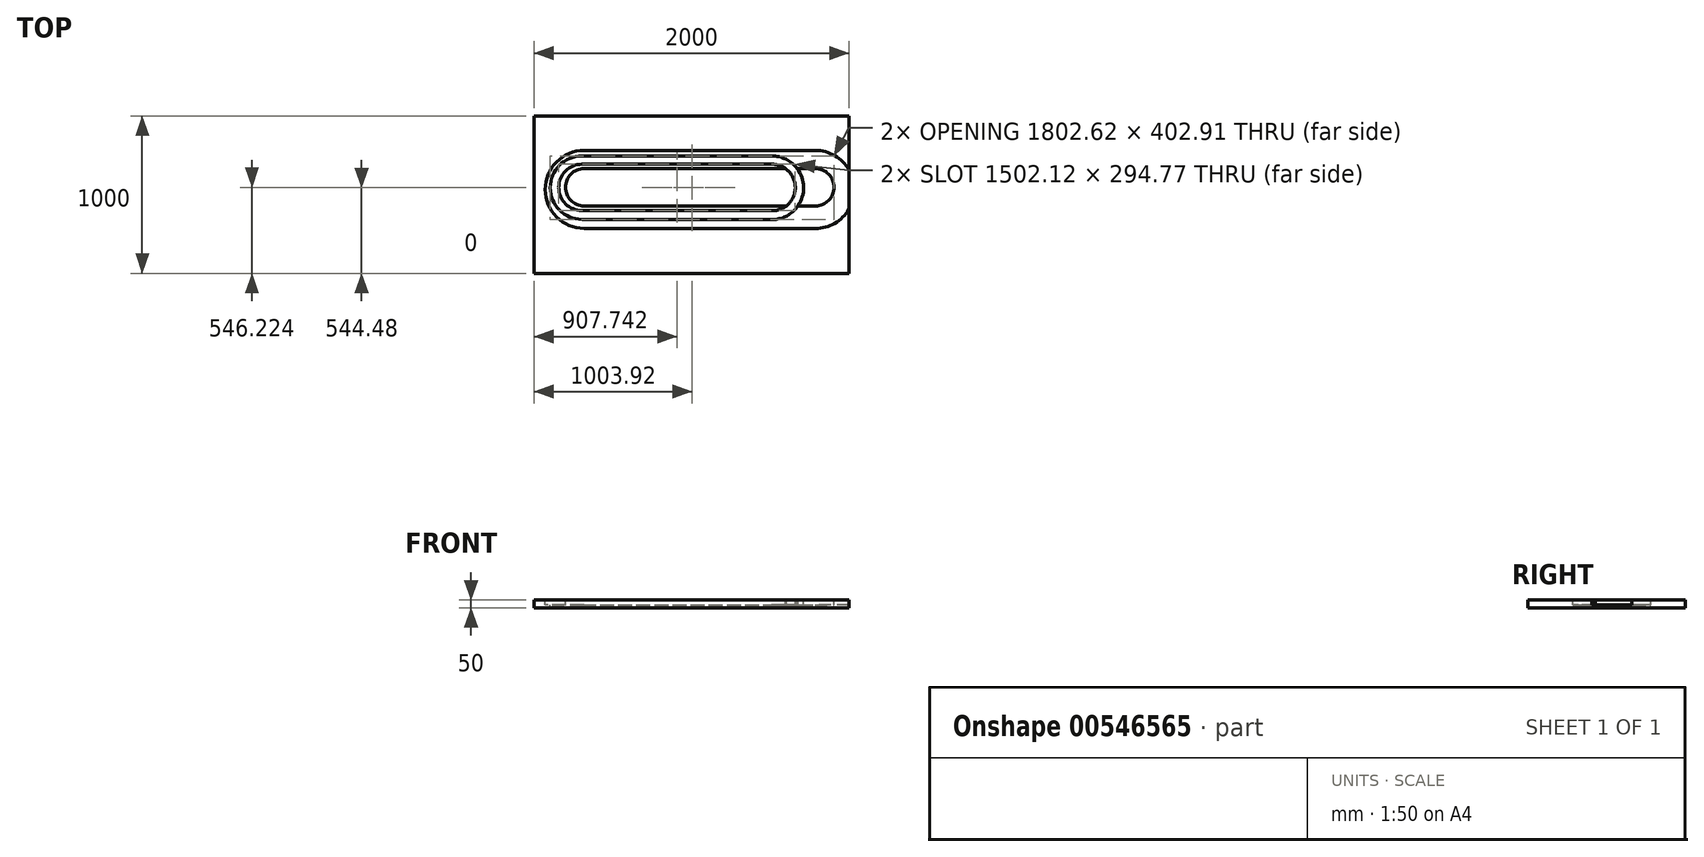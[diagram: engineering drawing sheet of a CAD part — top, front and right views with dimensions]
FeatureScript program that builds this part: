
annotation { "Feature Type Name" : "Feature", "Feature Type Description" : "" }
export const myFeature = defineFeature(function(context is Context, id is Id, definition is map)
    precondition{}
    {
        {
            var Q0;
            Q0=qCreatedBy(makeId("Top.planeOp"),FACE);
            var sketch = newSketch(context, id + "F0", { "sketchPlane" : qUnion([Q0])});
            skLineSegment(sketch, "E0.bottom", {"start": v(-970.21, 444.4) * mm, "end": v(1029.79, 444.4) * mm});
            skLineSegment(sketch, "E0.top", {"start": v(-970.21, -555.6) * mm, "end": v(1029.79, -555.6) * mm});
            skLineSegment(sketch, "E0.left", {"start": v(-970.21, 444.4) * mm, "end": v(-970.21, -555.6) * mm});
            skLineSegment(sketch, "E0.right", {"start": v(1029.79, 444.4) * mm, "end": v(1029.79, -555.6) * mm});
            skSolve(sketch);
        }
        {
            var Q0;
            Q0=makeQuery(id+"F0.imprint","IMPRINT",FACE,{"disambiguationData":[TD([[makeQuery(id+"F0.imprint","IMPRINT",EDGE,{"derivedFrom":sQuery(id+"F0.wireOp",EDGE,"E0.bottom")}),-1.0]])]});
            extrude(context, id + "F1", {"entities" : qUnion([Q0]), "depth" : 50 * mm, "offsetDistance" : 25 * mm});
        }
        {
            var Q0;
            Q0=makeQuery(id+"F1.opExtrude","CAP_FACE",FACE,{"disambiguationData":[OSD([sQuery(id+"F0.wireOp",EDGE,"E0.bottom"),sQuery(id+"F0.wireOp",EDGE,"E0.top"),sQuery(id+"F0.wireOp",EDGE,"E0.left"),sQuery(id+"F0.wireOp",EDGE,"E0.right")])],"isStart":false});
            var sketch = newSketch(context, id + "F2", { "sketchPlane" : qUnion([Q0])});
            skLineSegment(sketch, "E1.bottom", {"start": v(-652.19, 225.2) * mm, "end": v(816.42, 225.2) * mm});
            skLineSegment(sketch, "E1.top", {"start": v(-652.19, -270.14) * mm, "end": v(816.42, -270.14) * mm});
            skLineSegment(sketch, "E2", {"start": v(-652.19, -127.12) * mm, "end": v(816.42, -127.12) * mm});
            skLineSegment(sketch, "E3", {"start": v(-652.19, 110.1) * mm, "end": v(816.42, 110.1) * mm});
            skArc(sketch, "E4", {"start": v(-652.19, 225.2) * mm, "mid": v(-899.86, -22.47) * mm, "end": v(-652.19, -270.14) * mm});
            skArc(sketch, "E5", {"start": v(-652.19, 110.1) * mm, "mid": v(-770.8, -8.51) * mm, "end": v(-652.19, -127.12) * mm});
            skArc(sketch, "E6", {"start": v(816.42, 225.2) * mm, "mid": v(1064.1, -22.47) * mm, "end": v(816.42, -270.14) * mm});
            skArc(sketch, "E7", {"start": v(816.42, 110.1) * mm, "mid": v(935.02, -8.51) * mm, "end": v(816.42, -127.12) * mm});
            skSolve(sketch);
        }
        {
            var Q0;
            {var subQ1=sQuery(id+"F2.wireOp",EDGE,"E1.bottom");Q0=makeQuery(id+"F2.imprint","IMPRINT",FACE,{"disambiguationData":[TD([[makeQuery(id+"F2.imprint","IMPRINT",EDGE,{"derivedFrom":subQ1}),-1.0]])]});}
            extrude(context, id + "F3", {"entities" : qUnion([Q0]), "operationType" : NewBodyOperationType.REMOVE, "oppositeDirection" : true, "depth" : 30 * mm, "offsetDistance" : 25 * mm});
        }
        {
            var Q0;
            {var subQ0=sQuery(id+"F0.wireOp",EDGE,"E0.left");var subQ2=sQuery(id+"F0.wireOp",EDGE,"E0.top");var subQ3=sQuery(id+"F0.wireOp",EDGE,"E0.right");var subQ4=sQuery(id+"F0.wireOp",EDGE,"E0.bottom");Q0=makeQuery(id+"F3.boolean.opBoolean","SPLIT",FACE,{"disambiguationData":[TD([makeQuery(id+"F1.opExtrude","SWEPT_FACE",FACE,{"disambiguationData":[OSD([subQ4])]})])],"derivedFrom":makeQuery(id+"F1.opExtrude","CAP_FACE",FACE,{"disambiguationData":[OSD([subQ4,subQ2,subQ0,subQ3])],"isStart":false})});}
            var sketch = newSketch(context, id + "F4", { "sketchPlane" : qUnion([Q0])});
            skLineSegment(sketch, "E8", {"start": v(-666.14, 190.32) * mm, "end": v(539.1, 190.32) * mm});
            skLineSegment(sketch, "E9", {"start": v(-666.14, -156.77) * mm, "end": v(561.77, -156.77) * mm});
            skLineSegment(sketch, "E10", {"start": v(-666.14, 138) * mm, "end": v(540.84, 138) * mm});
            skLineSegment(sketch, "E11", {"start": v(-666.14, -212.58) * mm, "end": v(565.25, -212.58) * mm});
            skArc(sketch, "E12", {"start": v(-666.14, 190.32) * mm, "mid": v(-867.6, -11.13) * mm, "end": v(-666.14, -212.58) * mm});
            skArc(sketch, "E13", {"start": v(-666.14, 138) * mm, "mid": v(-813.53, -9.39) * mm, "end": v(-666.14, -156.77) * mm});
            skArc(sketch, "E14", {"start": v(540.84, 138) * mm, "mid": v(688.59, 0.36) * mm, "end": v(561.77, -156.77) * mm});
            skArc(sketch, "E15", {"start": v(539.1, 190.32) * mm, "mid": v(740.97, 1.13) * mm, "end": v(565.25, -212.58) * mm});
            skSolve(sketch);
        }
        {
            var Q0;
            Q0=makeQuery(id+"F4.imprint","IMPRINT",FACE,{"disambiguationData":[TD([[makeQuery(id+"F4.imprint","IMPRINT",EDGE,{"derivedFrom":sQuery(id+"F4.wireOp",EDGE,"E8")}),-1.0]])]});
            extrude(context, id + "F5", {"entities" : qUnion([Q0]), "operationType" : NewBodyOperationType.REMOVE, "oppositeDirection" : true, "depth" : 40 * mm, "offsetDistance" : 25 * mm});
        }
    });
